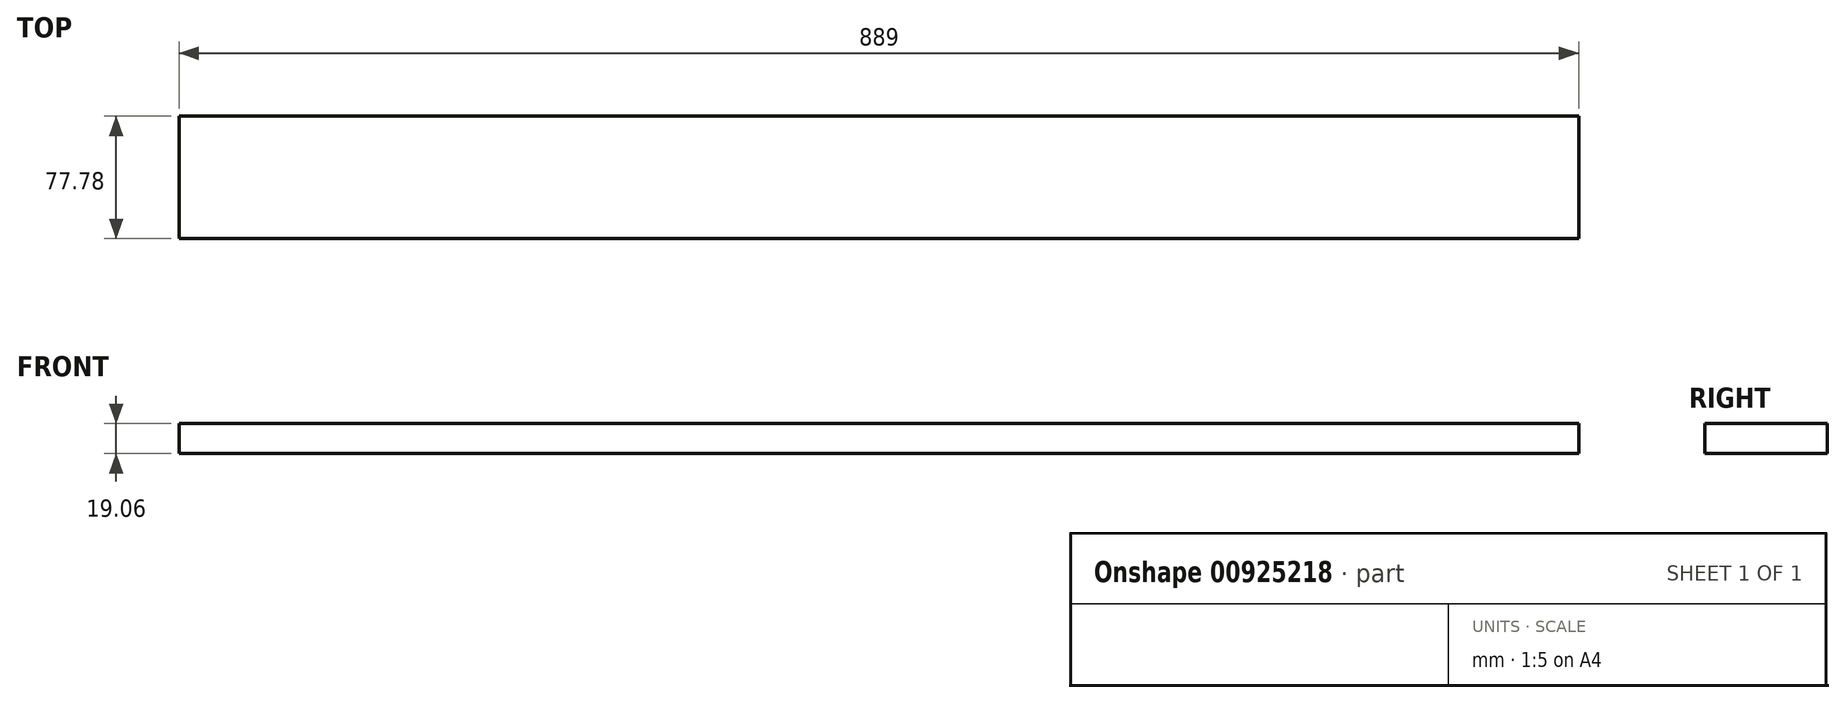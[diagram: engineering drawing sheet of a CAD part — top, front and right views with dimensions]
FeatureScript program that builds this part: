
annotation { "Feature Type Name" : "Feature", "Feature Type Description" : "" }
export const myFeature = defineFeature(function(context is Context, id is Id, definition is map)
    precondition{}
    {
        {
            var Q0;
            Q0=qCreatedBy(makeId("Right.planeOp"),FACE);
            var sketch = newSketch(context, id + "F0", { "sketchPlane" : qUnion([Q0])});
            skLineSegment(sketch, "E0.bottom", {"start": v(38.9, -9.52) * mm, "end": v(-38.9, -9.53) * mm});
            skLineSegment(sketch, "E0.top", {"start": v(38.9, 9.53) * mm, "end": v(-38.9, 9.52) * mm});
            skLineSegment(sketch, "E0.left", {"start": v(38.9, -9.52) * mm, "end": v(38.9, 9.53) * mm});
            skLineSegment(sketch, "E0.right", {"start": v(-38.9, -9.53) * mm, "end": v(-38.9, 9.52) * mm});
            skPoint(sketch, "E0.middle", {"position": v(0, 0) * mm});
            skSolve(sketch);
        }
        {
            var Q0;
            Q0=makeQuery(id+"F0.imprint","IMPRINT",FACE,{"disambiguationData":[TD([[makeQuery(id+"F0.imprint","IMPRINT",EDGE,{"derivedFrom":sQuery(id+"F0.wireOp",EDGE,"E0.bottom")}),-1.0]])]});
            extrude(context, id + "F1", {"entities" : qUnion([Q0]), "depth" : 889 * mm, "offsetDistance" : 25.4 * mm});
        }
    });
